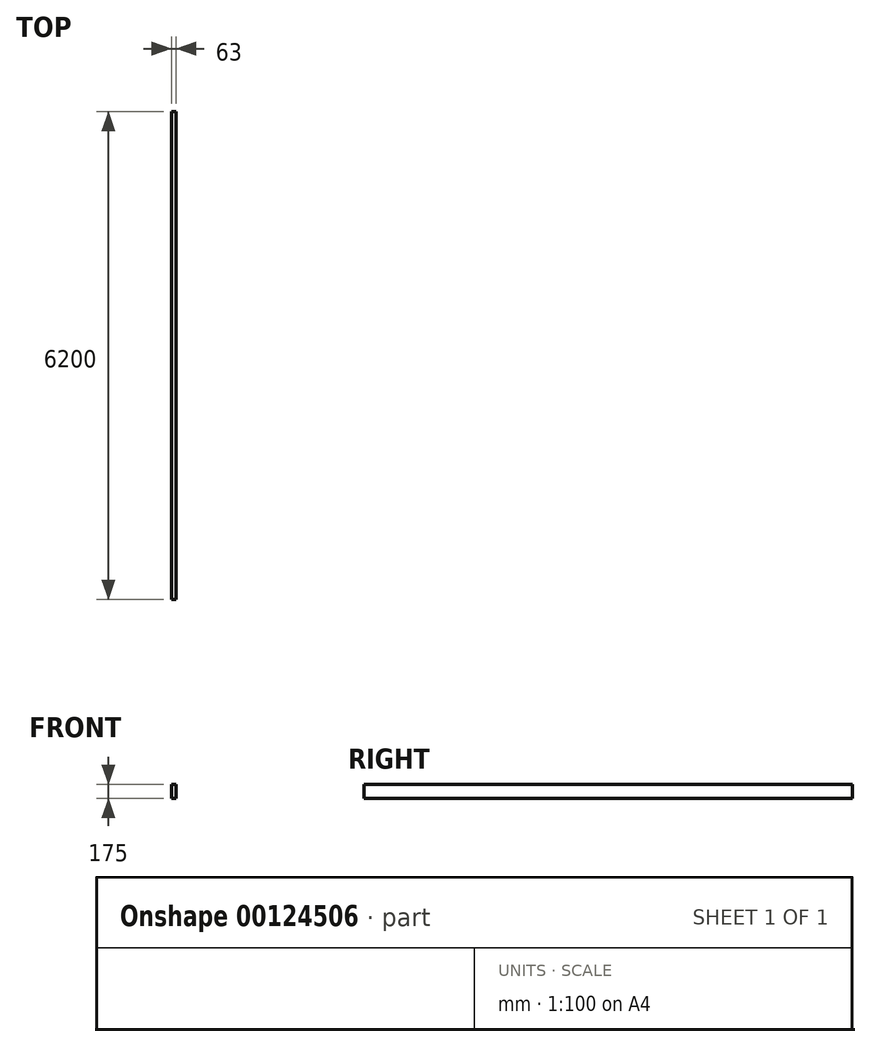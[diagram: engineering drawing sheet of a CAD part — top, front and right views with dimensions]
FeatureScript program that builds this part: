
annotation { "Feature Type Name" : "Feature", "Feature Type Description" : "" }
export const myFeature = defineFeature(function(context is Context, id is Id, definition is map)
    precondition{}
    {
        {
            var Q0;
            Q0=qCreatedBy(makeId("Front.planeOp"),FACE);
            var sketch = newSketch(context, id + "F0", { "sketchPlane" : qUnion([Q0])});
            skLineSegment(sketch, "E0.bottom", {"start": v(31.5, 87.5) * mm, "end": v(-31.5, 87.5) * mm});
            skLineSegment(sketch, "E0.top", {"start": v(31.5, -87.5) * mm, "end": v(-31.5, -87.5) * mm});
            skLineSegment(sketch, "E0.left", {"start": v(31.5, 87.5) * mm, "end": v(31.5, -87.5) * mm});
            skLineSegment(sketch, "E0.right", {"start": v(-31.5, 87.5) * mm, "end": v(-31.5, -87.5) * mm});
            skPoint(sketch, "E0.middle", {"position": v(0, 0) * mm});
            skSolve(sketch);
        }
        {
            var Q0;
            Q0 = qSketchRegion(id + "F0", true);
            extrude(context, id + "F1", {"entities" : qUnion([Q0]), "endBound" : BoundingType.SYMMETRIC, "depth" : 6200 * mm});
        }
    });
